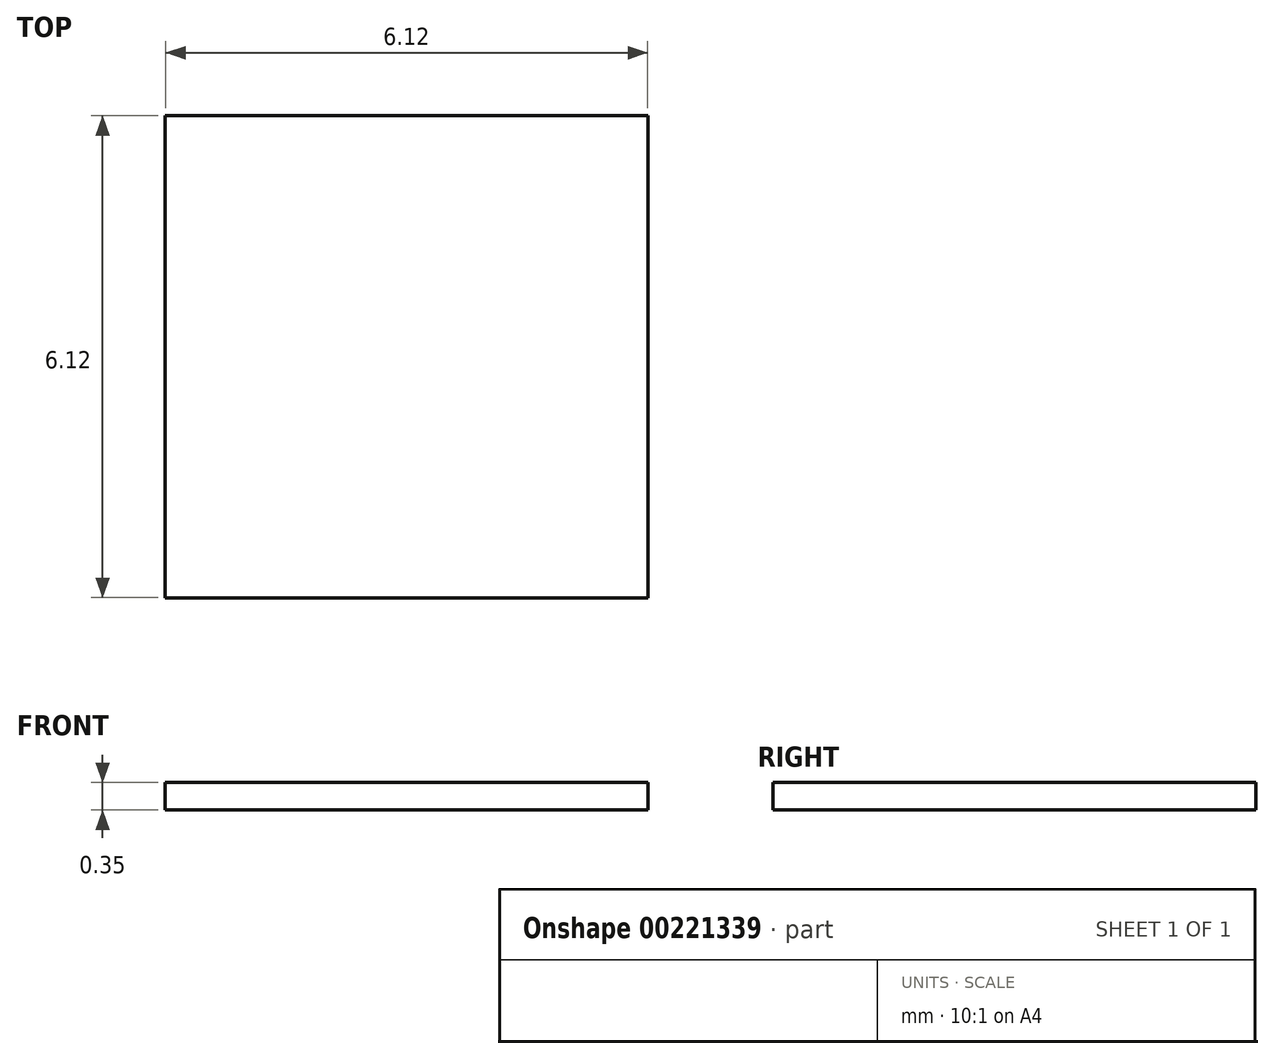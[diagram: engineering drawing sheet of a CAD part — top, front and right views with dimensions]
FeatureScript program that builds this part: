
annotation { "Feature Type Name" : "Feature", "Feature Type Description" : "" }
export const myFeature = defineFeature(function(context is Context, id is Id, definition is map)
    precondition{}
    {
        {
            var Q0;
            Q0=qCreatedBy(makeId("Top.planeOp"),FACE);
            var sketch = newSketch(context, id + "F0", { "sketchPlane" : qUnion([Q0])});
            skLineSegment(sketch, "E0.bottom", {"start": v(-3.06, 3.06) * mm, "end": v(3.06, 3.06) * mm});
            skLineSegment(sketch, "E0.top", {"start": v(-3.06, -3.06) * mm, "end": v(3.07, -3.06) * mm});
            skLineSegment(sketch, "E0.left", {"start": v(-3.06, 3.07) * mm, "end": v(-3.06, -3.06) * mm});
            skLineSegment(sketch, "E0.right", {"start": v(3.07, 3.06) * mm, "end": v(3.07, -3.06) * mm});
            skSolve(sketch);
        }
        {
            var Q0;
            Q0=makeQuery(id+"F0.imprint","IMPRINT",FACE,{"disambiguationData":[TD([[makeQuery(id+"F0.imprint","IMPRINT",EDGE,{"derivedFrom":sQuery(id+"F0.wireOp",EDGE,"E0.bottom")}),-1.0]])]});
            extrude(context, id + "F1", {"entities" : qUnion([Q0]), "depth" : 0.35 * mm});
        }
    });
